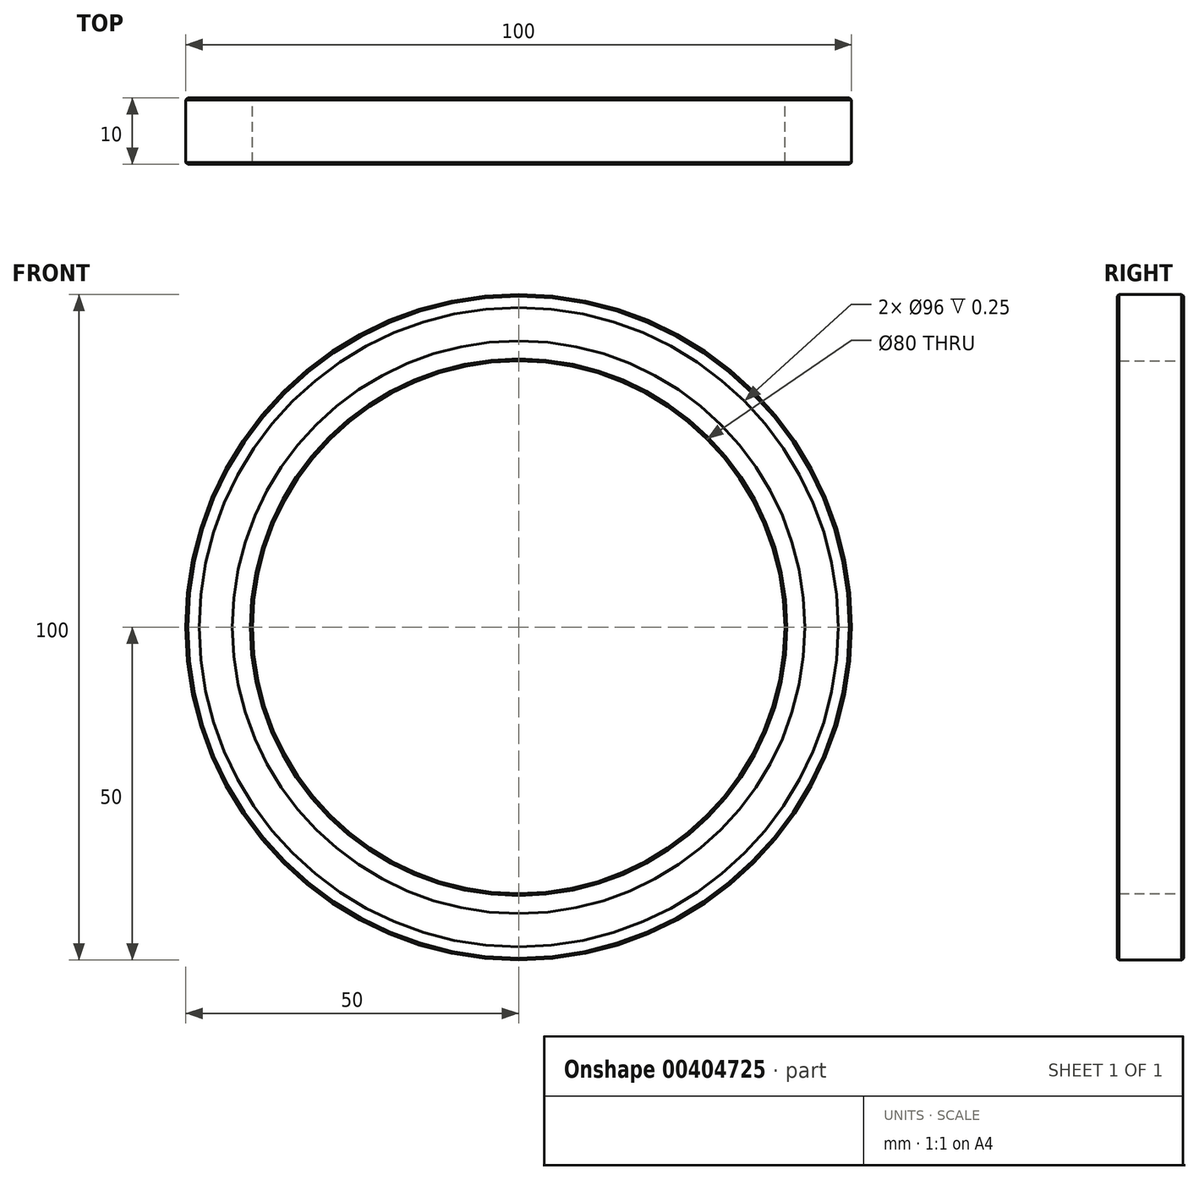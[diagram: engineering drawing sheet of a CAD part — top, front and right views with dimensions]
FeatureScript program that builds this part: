
annotation { "Feature Type Name" : "Feature", "Feature Type Description" : "" }
export const myFeature = defineFeature(function(context is Context, id is Id, definition is map)
    precondition{}
    {
        {
            var Q0;
            Q0=qCreatedBy(makeId("Front.planeOp"),FACE);
            var sketch = newSketch(context, id + "F0", { "sketchPlane" : qUnion([Q0])});
            skCircle(sketch, "E0", {"center": v(0, 0) * mm, "radius": 40 * mm});
            skCircle(sketch, "E1", {"center": v(0, 0) * mm, "radius": 43 * mm});
            skCircle(sketch, "E2", {"center": v(0, 0) * mm, "radius": 48 * mm});
            skCircle(sketch, "E3", {"center": v(0, 0) * mm, "radius": 50 * mm});
            skSolve(sketch);
        }
        {
            var Q0;
            Q0=makeQuery(id+"F0.imprint","IMPRINT",FACE,{"disambiguationData":[TD([[makeQuery(id+"F0.imprint","IMPRINT",EDGE,{"derivedFrom":sQuery(id+"F0.wireOp",EDGE,"E2")}),-1.0]])]});
            var Q1;
            Q1=makeQuery(id+"F0.imprint","IMPRINT",FACE,{"disambiguationData":[TD([[makeQuery(id+"F0.imprint","IMPRINT",EDGE,{"derivedFrom":sQuery(id+"F0.wireOp",EDGE,"E0")}),-1.0]])]});
            extrude(context, id + "F1", {"entities" : qUnion([Q0, Q1]), "flatOperationType" : FlatOperationType.REMOVE, "offsetDistance" : 25 * mm, "depth" : 10 * mm, "domain" : OperationDomain.MODEL, "symmetric" : true});
        }
        {
            var Q0;
            Q0=makeQuery(id+"F0.imprint","IMPRINT",FACE,{"disambiguationData":[TD([[makeQuery(id+"F0.imprint","IMPRINT",EDGE,{"derivedFrom":sQuery(id+"F0.wireOp",EDGE,"E1")}),-1.0]])]});
            extrude(context, id + "F2", {"entities" : qUnion([Q0]), "operationType" : NewBodyOperationType.ADD, "flatOperationType" : FlatOperationType.REMOVE, "offsetDistance" : 25 * mm, "depth" : 9.5 * mm, "domain" : OperationDomain.MODEL, "symmetric" : true});
        }
        {
            var Q0;
            Q0=makeQuery(id+"F1.opExtrude","SWEPT_FACE",FACE,{"disambiguationData":[OSD([sQuery(id+"F0.wireOp",EDGE,"E3")])]});
            var Q1;
            Q1=makeQuery(id+"F1.opExtrude","SWEPT_FACE",FACE,{"disambiguationData":[OSD([sQuery(id+"F0.wireOp",EDGE,"E0")])]});
            chamfer(context, id + "F3", {"entities" : qUnion([Q0, Q1]), "width" : 0.3 * mm, "tangentPropagation" : true});
        }
    });
